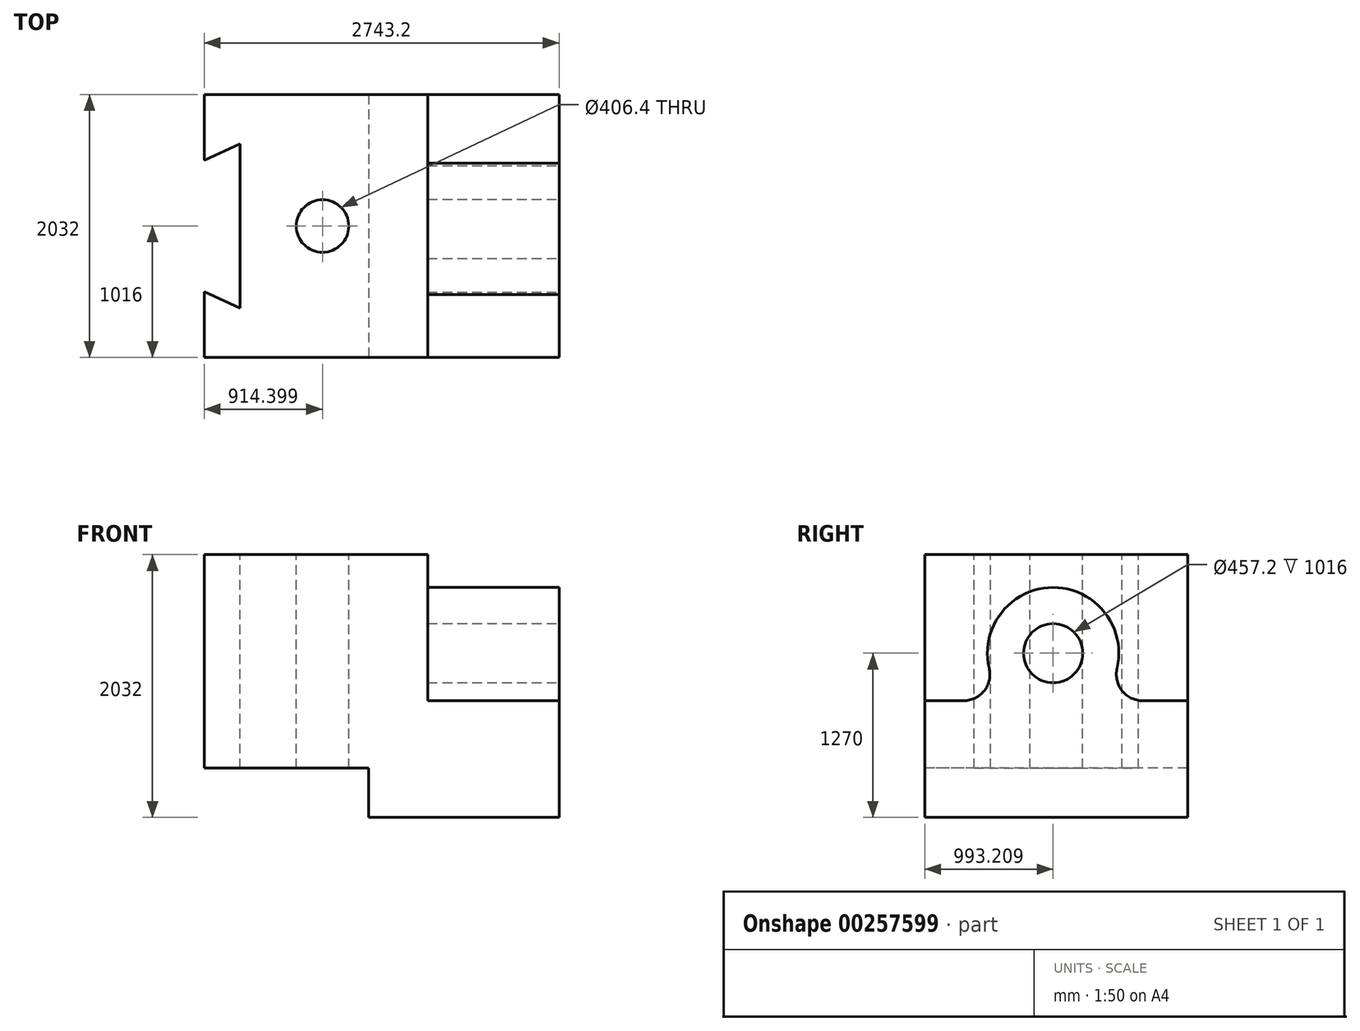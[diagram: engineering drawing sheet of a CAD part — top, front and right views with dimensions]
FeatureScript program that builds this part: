
annotation { "Feature Type Name" : "Feature", "Feature Type Description" : "" }
export const myFeature = defineFeature(function(context is Context, id is Id, definition is map)
    precondition{}
    {
        {
            var Q0;
            Q0=qCreatedBy(makeId("Front.planeOp"),FACE);
            var sketch = newSketch(context, id + "F0", { "sketchPlane" : qUnion([Q0])});
            skLineSegment(sketch, "E0", {"start": v(1233.45, -1176.65) * mm, "end": v(1233.45, -273.8) * mm});
            skLineSegment(sketch, "E1", {"start": v(1233.45, -273.8) * mm, "end": v(217.45, -273.8) * mm});
            skLineSegment(sketch, "E2", {"start": v(217.45, -273.8) * mm, "end": v(217.45, 855.35) * mm});
            skLineSegment(sketch, "E3", {"start": v(-1509.75, -795.65) * mm, "end": v(-239.75, -795.65) * mm});
            skLineSegment(sketch, "E4", {"start": v(-239.75, -795.65) * mm, "end": v(-239.75, -1176.65) * mm});
            skLineSegment(sketch, "E5", {"start": v(-239.75, -1176.65) * mm, "end": v(1233.45, -1176.65) * mm});
            skLineSegment(sketch, "E6", {"start": v(217.45, 855.35) * mm, "end": v(-1509.75, 855.35) * mm});
            skLineSegment(sketch, "E7", {"start": v(-1509.75, -795.65) * mm, "end": v(-1509.75, 855.35) * mm});
            skSolve(sketch);
        }
        {
            var Q0;
            Q0 = qSketchRegion(id + "F0", true);
            extrude(context, id + "F1", {"entities" : qUnion([Q0]), "oppositeDirection" : true, "depth" : 2032 * mm});
        }
        {
            var Q0;
            Q0=makeQuery(id+"F1.opExtrude","SWEPT_FACE",FACE,{"disambiguationData":[OSD([sQuery(id+"F0.wireOp",EDGE,"E6")])]});
            var sketch = newSketch(context, id + "F2", { "sketchPlane" : qUnion([Q0])});
            skLineSegment(sketch, "E8", {"start": v(-1232.67, 1651) * mm, "end": v(-1509.75, 1524) * mm});
            skLineSegment(sketch, "E9", {"start": v(-1509.75, 1524) * mm, "end": v(-1509.75, 2032) * mm});
            skLineSegment(sketch, "E10", {"start": v(-1509.75, 2032) * mm, "end": v(-2309.39, 1178.27) * mm});
            skLineSegment(sketch, "E11", {"start": v(-2309.39, 1178.27) * mm, "end": v(-2251.44, 691.47) * mm});
            skLineSegment(sketch, "E12", {"start": v(-2251.44, 691.47) * mm, "end": v(-1509.75, 0) * mm});
            skLineSegment(sketch, "E13", {"start": v(-1509.75, 0) * mm, "end": v(-1509.75, 508) * mm});
            skLineSegment(sketch, "E14", {"start": v(-1509.75, 1016) * mm, "end": v(1567.63, 1016) * mm, "construction": true});
            skPoint(sketch, "E14.endSnap0", {"position": v(217.45, 1016) * mm});
            skLineSegment(sketch, "E15.MirrorCS", {"start": v(-1232.67, 381) * mm, "end": v(-1509.75, 508) * mm});
            skLineSegment(sketch, "E16", {"start": v(-1232.67, 381) * mm, "end": v(-1232.67, 1651) * mm});
            skSolve(sketch);
        }
        {
            var Q0;
            Q0 = qSketchRegion(id + "F2", true);
            extrude(context, id + "F3", {"entities" : qUnion([Q0]), "operationType" : NewBodyOperationType.REMOVE, "oppositeDirection" : true, "depth" : 1651 * mm});
        }
        {
            var Q0;
            Q0=makeQuery(id+"F1.opExtrude","SWEPT_FACE",FACE,{"disambiguationData":[OSD([sQuery(id+"F0.wireOp",EDGE,"E6")])]});
            var sketch = newSketch(context, id + "F4", { "sketchPlane" : qUnion([Q0])});
            skCircle(sketch, "E17", {"center": v(-595.35, 1016) * mm, "radius": 203.2 * mm});
            skLineSegment(sketch, "E18", {"start": v(-1232.67, 1016) * mm, "end": v(1814.47, 1016) * mm, "construction": true});
            skSolve(sketch);
        }
        {
            var Q0;
            Q0 = qSketchRegion(id + "F4", true);
            extrude(context, id + "F5", {"entities" : qUnion([Q0]), "operationType" : NewBodyOperationType.REMOVE, "oppositeDirection" : true, "depth" : 1651 * mm});
        }
        {
            var Q0;
            Q0=makeQuery(id+"F1.opExtrude","SWEPT_FACE",FACE,{"disambiguationData":[OSD([sQuery(id+"F0.wireOp",EDGE,"E0")])]});
            var sketch = newSketch(context, id + "F6", { "sketchPlane" : qUnion([Q0])});
            skCircle(sketch, "E19", {"center": v(993.2, 93.35) * mm, "radius": 508 * mm});
            skLineSegment(sketch, "E20", {"start": v(485.2, 93.35) * mm, "end": v(485.2, -273.8) * mm});
            skLineSegment(sketch, "E21", {"start": v(1501.2, 93.35) * mm, "end": v(1501.2, -447.06) * mm});
            skSolve(sketch);
        }
        {
            var Q0;
            Q0 = qSketchRegion(id + "F6", true);
            extrude(context, id + "F7", {"entities" : qUnion([Q0]), "operationType" : NewBodyOperationType.ADD, "oppositeDirection" : true, "depth" : 1016 * mm});
        }
        {
            var Q0;
            Q0=makeQuery(id+"F7.boolean.opBoolean","INTERSECT",EDGE,{"disambiguationData":[OD(0.0)],"derivedFrom":[makeQuery(id+"F1.opExtrude","SWEPT_FACE",FACE,{"disambiguationData":[OSD([sQuery(id+"F0.wireOp",EDGE,"E1")])]}),makeQuery(id+"F7.opExtrude","SWEPT_FACE",FACE,{"disambiguationData":[OSD([sQuery(id+"F6.wireOp",EDGE,"E19")])]})]});
            fillet(context, id + "F8", {"entities" : qUnion([Q0]), "radius" : 203.2 * mm, "tangentPropagation" : true, "allowEdgeOverflow" : false});
        }
        {
            var Q0;
            Q0=makeQuery(id+"F7.boolean.opBoolean","INTERSECT",EDGE,{"disambiguationData":[OD(1.0)],"derivedFrom":[makeQuery(id+"F1.opExtrude","SWEPT_FACE",FACE,{"disambiguationData":[OSD([sQuery(id+"F0.wireOp",EDGE,"E1")])]}),makeQuery(id+"F7.opExtrude","SWEPT_FACE",FACE,{"disambiguationData":[OSD([sQuery(id+"F6.wireOp",EDGE,"E19")])]})]});
            fillet(context, id + "F9", {"entities" : qUnion([Q0]), "radius" : 203.2 * mm, "tangentPropagation" : true, "allowEdgeOverflow" : false});
        }
        {
            var Q0;
            Q0=makeQuery(id+"F7.boolean.opBoolean","MERGE",FACE,{"derivedFrom":[makeQuery(id+"F1.opExtrude","SWEPT_FACE",FACE,{"disambiguationData":[OSD([sQuery(id+"F0.wireOp",EDGE,"E0")])]}),makeQuery(id+"F7.opExtrude","CAP_FACE",FACE,{"disambiguationData":[OSD([sQuery(id+"F6.wireOp",EDGE,"E19")])],"isStart":true})]});
            var sketch = newSketch(context, id + "F10", { "sketchPlane" : qUnion([Q0])});
            skCircle(sketch, "E22", {"center": v(993.2, 93.35) * mm, "radius": 228.6 * mm});
            skSolve(sketch);
        }
        {
            var Q0;
            Q0 = qSketchRegion(id + "F10", true);
            extrude(context, id + "F11", {"entities" : qUnion([Q0]), "operationType" : NewBodyOperationType.ADD, "oppositeDirection" : true, "depth" : 1016 * mm});
        }
        {
            var Q0;
            Q0=makeQuery(id+"F7.boolean.opBoolean","MERGE",FACE,{"derivedFrom":[makeQuery(id+"F1.opExtrude","SWEPT_FACE",FACE,{"disambiguationData":[OSD([sQuery(id+"F0.wireOp",EDGE,"E0")])]}),makeQuery(id+"F7.opExtrude","CAP_FACE",FACE,{"disambiguationData":[OSD([sQuery(id+"F6.wireOp",EDGE,"E19")])],"isStart":true})]});
            var sketch = newSketch(context, id + "F12", { "sketchPlane" : qUnion([Q0])});
            skCircle(sketch, "E23", {"center": v(993.2, 93.35) * mm, "radius": 228.6 * mm});
            skSolve(sketch);
        }
        {
            var Q0;
            Q0 = qSketchRegion(id + "F12", true);
            extrude(context, id + "F13", {"entities" : qUnion([Q0]), "operationType" : NewBodyOperationType.REMOVE, "oppositeDirection" : true, "depth" : 1016 * mm});
        }
    });
